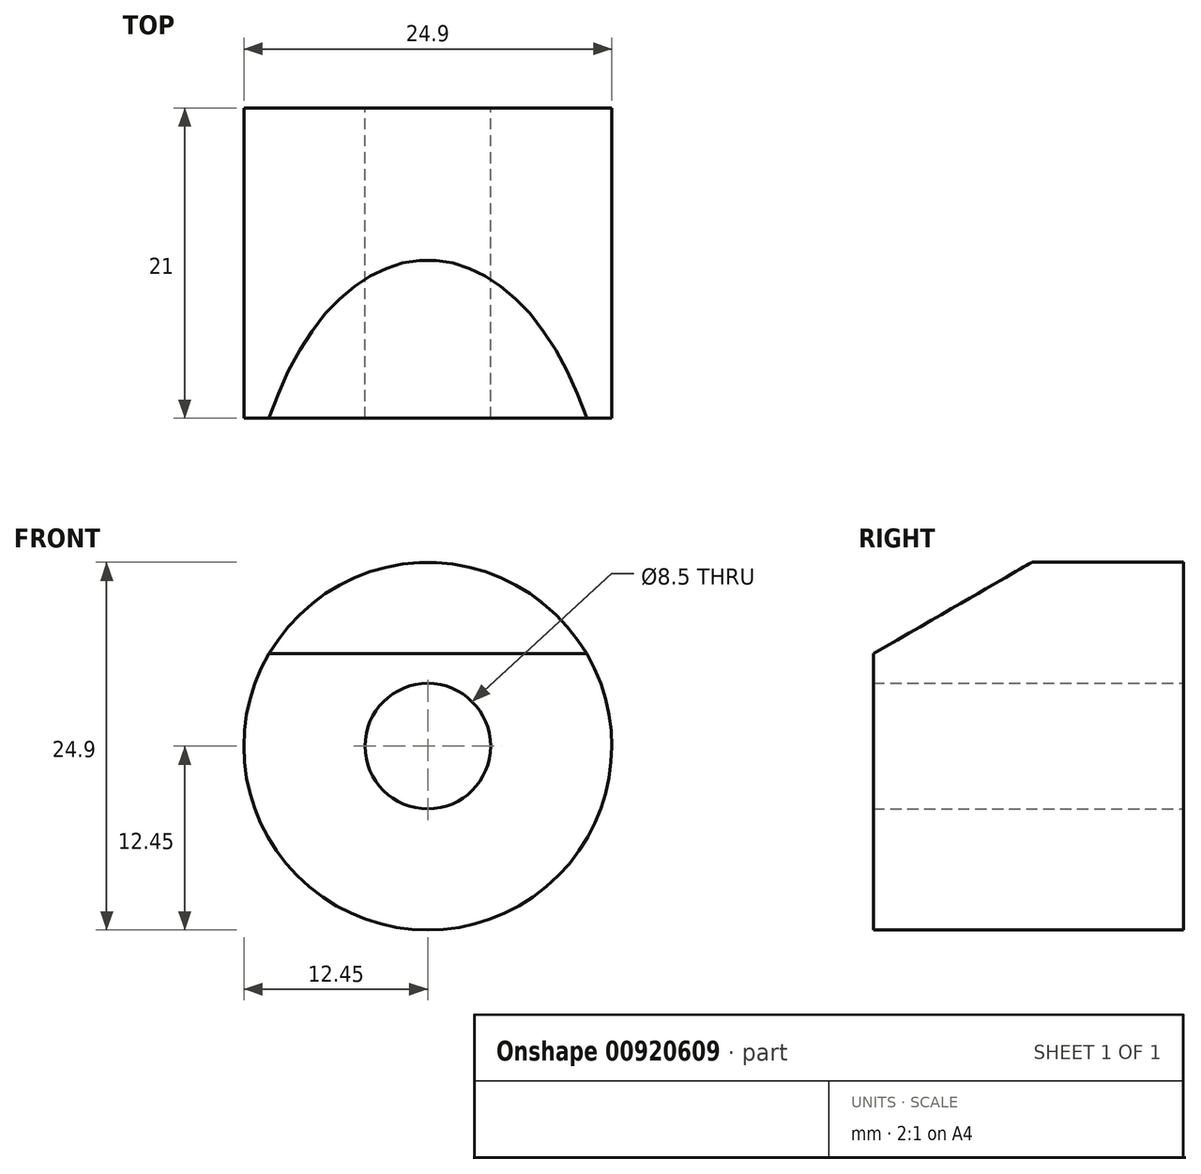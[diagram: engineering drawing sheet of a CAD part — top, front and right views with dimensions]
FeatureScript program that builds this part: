
annotation { "Feature Type Name" : "Feature", "Feature Type Description" : "" }
export const myFeature = defineFeature(function(context is Context, id is Id, definition is map)
    precondition{}
    {
        {
            var Q0;
            Q0=qCreatedBy(makeId("Front.planeOp"),FACE);
            var sketch = newSketch(context, id + "F0", { "sketchPlane" : qUnion([Q0])});
            skCircle(sketch, "E0", {"center": v(0, 0) * mm, "radius": 4.25 * mm});
            skCircle(sketch, "E1", {"center": v(0, 0) * mm, "radius": 12.45 * mm});
            skSolve(sketch);
        }
        {
            var Q0;
            Q0=makeQuery(id+"F0.imprint","IMPRINT",FACE,{"disambiguationData":[TD([[makeQuery(id+"F0.imprint","IMPRINT",EDGE,{"derivedFrom":sQuery(id+"F0.wireOp",EDGE,"E0")}),-1.0]])]});
            extrude(context, id + "F1", {"entities" : qUnion([Q0]), "depth" : 21 * mm, "offsetDistance" : 25 * mm});
        }
        {
            var Q0;
            Q0=qCreatedBy(makeId("Right.planeOp"),FACE);
            var sketch = newSketch(context, id + "F2", { "sketchPlane" : qUnion([Q0])});
            skLineSegment(sketch, "E2", {"start": v(-21, 12.45) * mm, "end": v(0, 12.45) * mm, "construction": true});
            skLineSegment(sketch, "E3", {"start": v(0, -12.45) * mm, "end": v(-21, -12.45) * mm, "construction": true});
            skLineSegment(sketch, "E4", {"start": v(-21, -12.45) * mm, "end": v(-21, 12.45) * mm, "construction": true});
            skLineSegment(sketch, "E5", {"start": v(-21, 12.45) * mm, "end": v(-21, 6.25) * mm});
            skLineSegment(sketch, "E6", {"start": v(-21, 12.45) * mm, "end": v(-10.26, 12.45) * mm});
            skLineSegment(sketch, "E7", {"start": v(-21, 6.25) * mm, "end": v(-10.26, 12.45) * mm});
            skSolve(sketch);
        }
        {
            var Q0;
            Q0=makeQuery(id+"F2.imprint","IMPRINT",FACE,{"disambiguationData":[TD([[makeQuery(id+"F2.imprint","IMPRINT",EDGE,{"derivedFrom":sQuery(id+"F2.wireOp",EDGE,"E5")}),1.0]])]});
            extrude(context, id + "F3", {"entities" : qUnion([Q0]), "operationType" : NewBodyOperationType.REMOVE, "oppositeDirection" : true, "depth" : 25 * mm, "offsetDistance" : 25 * mm, "symmetric" : true});
        }
    });
